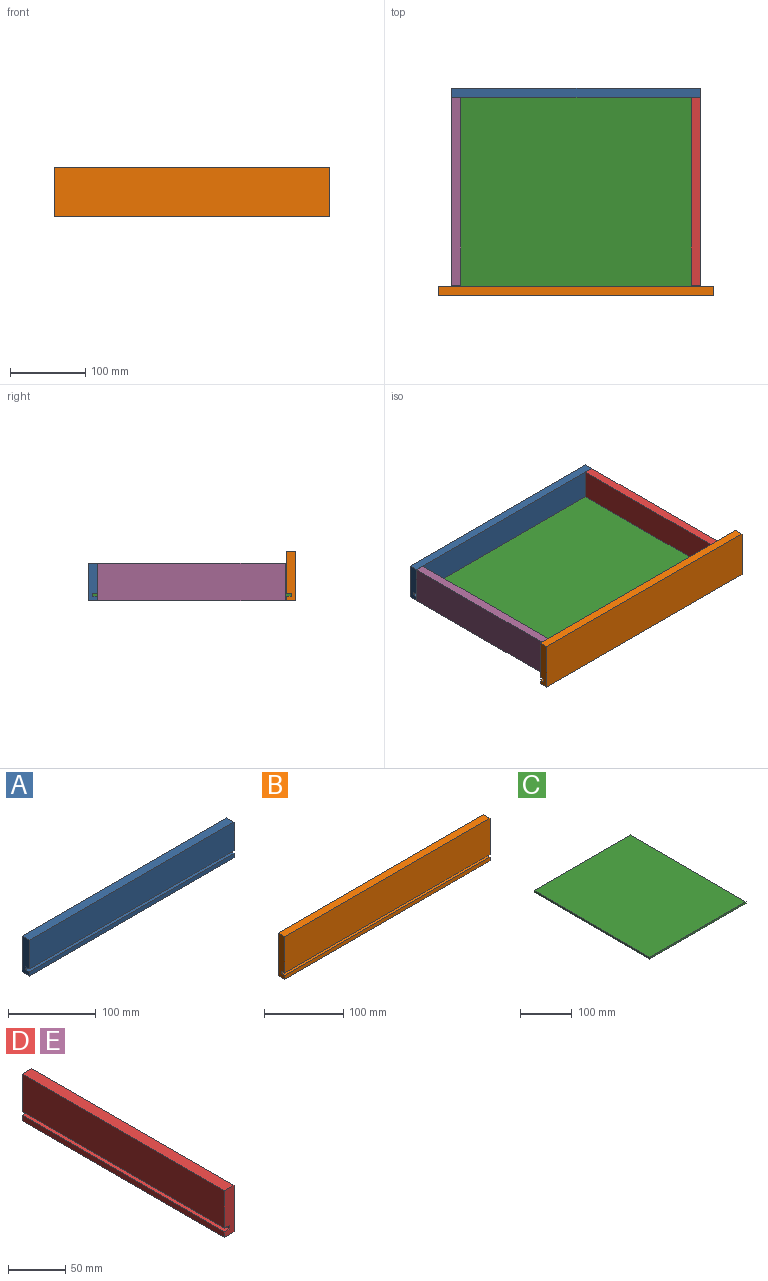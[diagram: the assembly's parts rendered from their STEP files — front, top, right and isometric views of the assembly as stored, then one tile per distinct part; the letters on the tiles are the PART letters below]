
ASSEMBLY  parts=5 mates=4
PART A: 10 faces, bbox 330x12x50 mm
  f0: plane 330x40mm, normal (0,-1,0), area 13200mm2, adj f1,f2,f4,f7
  f1: plane 50x12mm, normal (1,0,0), area 576mm2, adj f0,f3,f4,f5,f6,f7,f8,f9
  f2: plane 50x12mm, normal (-1,0,0), area 576mm2, adj f0,f3,f4,f5,f6,f7,f8,f9
  f3: plane 330x12mm, normal (0,0,-1), area 3960mm2, adj f1,f2,f5,f6
  f4: plane 330x12mm, normal (0,0,1), area 3960mm2, adj f0,f1,f2,f6
  f5: plane 330x6mm, normal (0,-1,0), area 1980mm2, adj f1,f2,f3,f8
  f6: plane 330x50mm, normal (0,1,0), area 16500mm2, adj f1,f2,f3,f4
  f7: plane 330x6mm, normal (0,0,-1), area 1980mm2, adj f0,f1,f2,f9
  f8: plane 330x6mm, normal (0,0,1), area 1980mm2, adj f1,f2,f5,f9
  f9: plane 330x4mm, normal (0,-1,0), area 1320mm2, adj f1,f2,f7,f8
PART B: 10 faces, bbox 367x12x66 mm
  f0: plane 367x56mm, normal (0,-1,0), area 20552mm2, adj f1,f2,f3,f7
  f1: plane 66x12mm, normal (1,0,0), area 768mm2, adj f0,f2,f4,f5,f6,f7,f8,f9
  f2: plane 367x12mm, normal (0,0,1), area 4404mm2, adj f0,f1,f3,f6
  f3: plane 66x12mm, normal (-1,0,0), area 768mm2, adj f0,f2,f4,f5,f6,f7,f8,f9
  f4: plane 367x12mm, normal (0,0,-1), area 4404mm2, adj f1,f3,f5,f6
  f5: plane 367x6mm, normal (0,-1,0), area 2202mm2, adj f1,f3,f4,f8
  f6: plane 367x66mm, normal (0,1,0), area 24222mm2, adj f1,f2,f3,f4
  f7: plane 367x6mm, normal (0,0,-1), area 2202mm2, adj f0,f1,f3,f9
  f8: plane 367x6mm, normal (0,0,1), area 2202mm2, adj f1,f3,f5,f9
  f9: plane 367x4mm, normal (0,-1,0), area 1468mm2, adj f1,f3,f7,f8
PART C: 6 faces, bbox 264x318x4 mm
  f0: plane 264x4mm, normal (0,1,0), area 1056mm2, adj f1,f3,f4,f5
  f1: plane 318x4mm, normal (-1,0,0), area 1272mm2, adj f0,f2,f4,f5
  f2: plane 264x4mm, normal (0,-1,0), area 1056mm2, adj f1,f3,f4,f5
  f3: plane 318x4mm, normal (1,0,0), area 1272mm2, adj f0,f2,f4,f5
  f4: plane 318x264mm, normal (0,0,1), area 83952mm2, adj f0,f1,f2,f3
  f5: plane 318x264mm, normal (0,0,-1), area 83952mm2, adj f0,f1,f2,f3
PART D: 10 faces, bbox 12x250x50 mm
  f0: plane 250x6mm, normal (-1,0,0), area 1500mm2, adj f1,f3,f4,f7
  f1: plane 50x12mm, normal (0,1,0), area 576mm2, adj f0,f2,f4,f5,f6,f7,f8,f9
  f2: plane 250x12mm, normal (0,0,1), area 3000mm2, adj f1,f3,f5,f6
  f3: plane 50x12mm, normal (0,-1,0), area 576mm2, adj f0,f2,f4,f5,f6,f7,f8,f9
  f4: plane 250x12mm, normal (0,0,-1), area 3000mm2, adj f0,f1,f3,f5
  f5: plane 250x50mm, normal (1,0,0), area 12500mm2, adj f1,f2,f3,f4
  f6: plane 250x40mm, normal (-1,0,0), area 10000mm2, adj f1,f2,f3,f8
  f7: plane 250x6mm, normal (0,0,1), area 1500mm2, adj f0,f1,f3,f9
  f8: plane 250x6mm, normal (0,0,-1), area 1500mm2, adj f1,f3,f6,f9
  f9: plane 250x4mm, normal (-1,0,0), area 1000mm2, adj f1,f3,f7,f8
PART E: same geometry as D
PLACE A t=(46.62,341.68,16.16)mm
PLACE B rot(axis=(0,0,1),180deg) t=(46.62,65.68,11.66)mm
PLACE C rot(axis=(0,0,1),90deg) t=(46.62,203.68,-15.34)mm
PLACE D t=(199.62,204.68,16.16)mm
PLACE E rot(axis=(0,0,-1),180deg) t=(-106.38,204.68,16.16)mm
MATE fastened D.f9 <-> C.f2  axis (-1,0,0) through (205.62,204.68,-13.34)mm
MATE fastened B.f9 <-> C.f1  axis (0,1,0) through (46.62,71.68,-13.34)mm
MATE fastened C.f3 <-> A.f9  axis (0,1,0) through (46.62,335.68,-13.34)mm
MATE fastened E.f9 <-> C.f0  axis (1,0,0) through (-112.38,204.68,-13.34)mm
